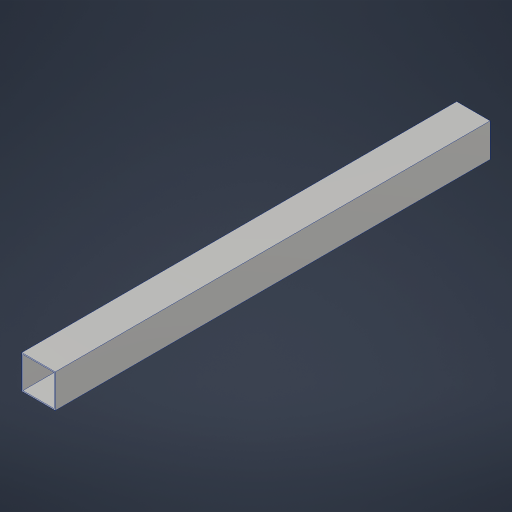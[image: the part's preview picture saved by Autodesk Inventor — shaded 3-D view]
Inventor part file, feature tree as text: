
AUTODESK INVENTOR PART (.ipt)
format: ipt  version: 2023.4 (Build 274418000, 418)  size: 170,496 bytes
history: native  units: in
note: dims shown in document units (in); Inventor stores cm internally (conversion verified against a paired STEP export)
features: extrude x1
ambient origin geometry x8: Origin, YZ Plane, XZ Plane, XY Plane, X Axis, Y Axis, Z Axis, Center Point
bodies: Solid1 (feature_tree)
feature tree (1):
  extrude  "Extrusion1"  TaperAngle=0.0deg  [1 undecoded]
note: 1 required parameter value undecoded (feature->parameter linkage not recoverable at this tier; creation-order binding heuristic only, values carry confidence <= 0.55)
